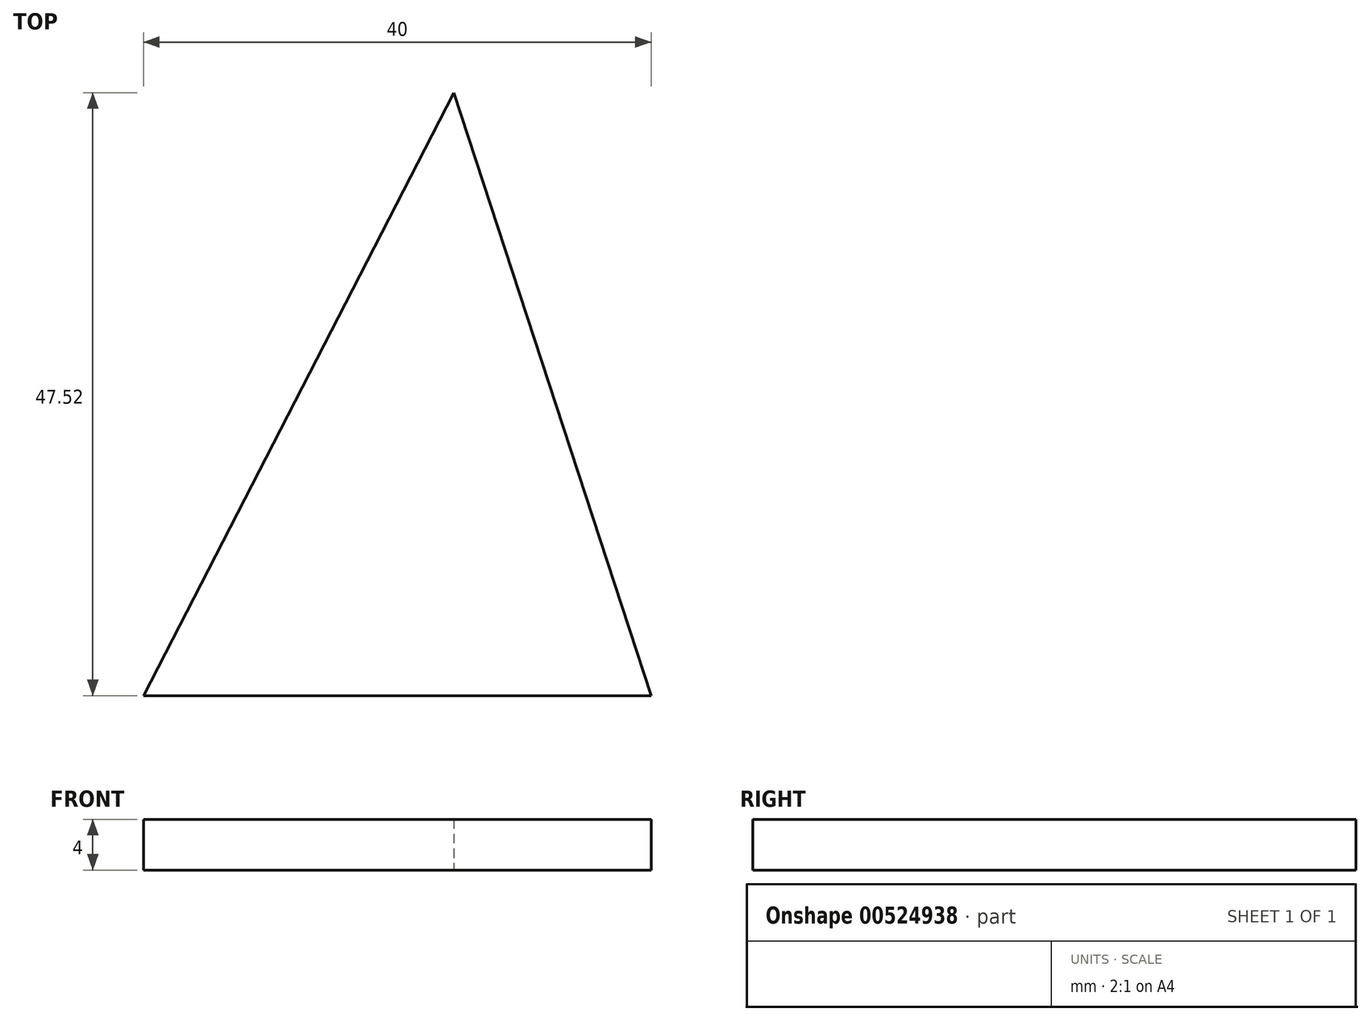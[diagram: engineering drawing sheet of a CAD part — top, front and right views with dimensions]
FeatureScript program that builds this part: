
annotation { "Feature Type Name" : "Feature", "Feature Type Description" : "" }
export const myFeature = defineFeature(function(context is Context, id is Id, definition is map)
    precondition{}
    {
        {
            var Q0;
            Q0=qCreatedBy(makeId("Top.planeOp"),FACE);
            var sketch = newSketch(context, id + "F0", { "sketchPlane" : qUnion([Q0])});
            skLineSegment(sketch, "E0", {"start": v(-40, 0) * mm, "end": v(-15.54, 47.52) * mm});
            skLineSegment(sketch, "E1", {"start": v(-15.54, 47.52) * mm, "end": v(0, 0) * mm});
            skLineSegment(sketch, "E2", {"start": v(0, 0) * mm, "end": v(-40, 0) * mm});
            skSolve(sketch);
        }
        {
            var Q0;
            Q0 = qSketchRegion(id + "F0", true);
            extrude(context, id + "F1", {"entities" : qUnion([Q0]), "depth" : 4 * mm, "offsetDistance" : 25 * mm});
        }
    });
